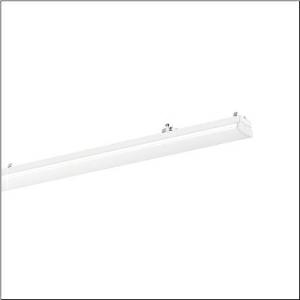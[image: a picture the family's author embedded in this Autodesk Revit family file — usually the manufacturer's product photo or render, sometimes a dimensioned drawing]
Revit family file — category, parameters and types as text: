
# Revit family: licross_r__11_recessed_opal_mo_51tl1dmn46xg_2fc5
name_source: partatom
category: Lighting Fixtures
units: mm (PartAtom-declared; Revit-internal decimal feet)

## family parameters
Cut with Voids When Loaded = No
Host = Face
Light Source = No
Part Type = Normal
Room Calculation Point = No
Round Connector Dimension = Use Diameter
Shared = No

## types (1)
- --- (1 x LED, 6320 lm, 34.3 W, 4000K)
    Apparent Load = 34 VA
    CIE Flux Codes = 44 73 91 87 100
    Color Rendering = 80
    Color Temperature = 4000K
    Default Elevation = 1800 mm
    Description = Licross® 11 recessed opal MO, luminaire insert, of sheet steel, coil coated, white, length: 1.500mm, width: 76mm, height: 87mm, LED rated luminous flux: 6.320lm, light colour: 840, control gear: ON/OFF Multilumen, with plug, 3-pole, with phase selection, mains connection: 220..240V, AC, 50/60Hz, rated input power: 34W, internal wiring halogen-free, primary optical cover: cover, of PMMA, light emission: direct with ceiling illumination distribution, primary light characteristic: symmetric, protection rating (complete): IP40, insulation class (complete): insulation class I (protective earthing), certification: CE, ENEC, VDE, UKCA, protection symbol: D if used in an environment without relevant dust loads with corresponding accessories, impact resistance: IK06, permissible ambient temperature for indoor applications: -35..+50°C, corresponds to IFS (International Featured Standards) requirements for safety and quality in the food industry, reducing of maximum allowable ambient temperature of 5°C with ceiling mounting, packaging unit: 1 piece
    Height = 83 mm
    Lamp = 1 x LED
    Lamp Light Flux = 6320 lm
    Lamp Power = 34.3 W
    Lamp count = 1
    Length = 1500 mm
    Luminous efficacy = 184 lm/W
    Manufacturer = Siteco
    ModVariant = No
    Model = 51TL1DMN46XG
    Mounting Place = Ceiling
    Mounting Type = Pendant
    Number of Poles = 1
    OnlyDefault = Yes
    Power Factor = 1
    Product Name = Licross® 11 recessed opal MO
    Product group = luminaire insert | ceiling pendant
    ProductGroupID = 902
    Protection Class = Protection class I
    Protection Degree = IP 40
    RLX_Detail_Level = 1
    RLX_Emergency_Light_Flux = 0 lm
    RLX_Emergency_Type = 0
    RLX_Emergency_Type_DB = No
    RlxData = <blob elided: 24633 chars, md5=c1249f50>
    Socket = socket
    Standby Power = 0 W
    System Light Flux = 6320 lm
    System Power = 34 W
    Type Comments = factory setting: luminous flux: 100 % | (A | C | E) | 79 mA
    Type Image = l_1313666.jpg
    URL = http://relux.com
    VarID = @adj_084473
    Voltage = 0 V
    Weight = 0.00 kg
    Width = 76 mm

## geometry (parser evidence)
native form markers: Blend x4, Sweep x12
no freeform markers — native parametric forms only
